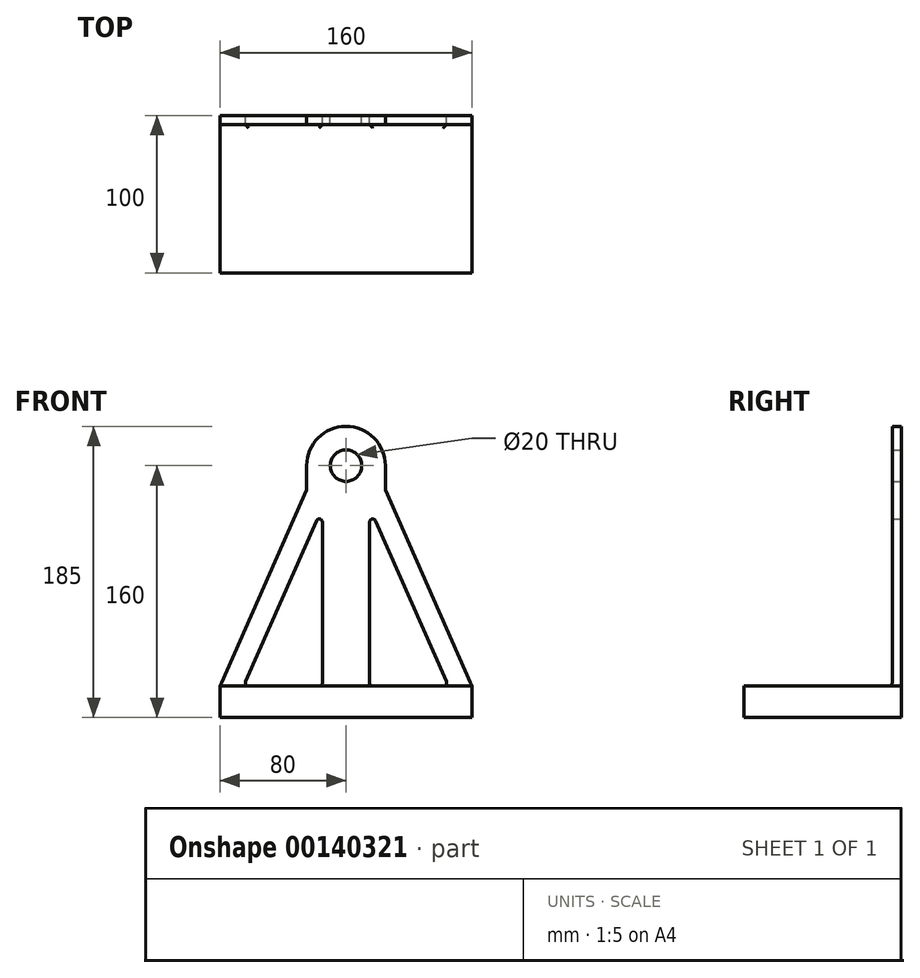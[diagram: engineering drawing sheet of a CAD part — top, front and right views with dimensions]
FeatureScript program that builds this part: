
annotation { "Feature Type Name" : "Feature", "Feature Type Description" : "" }
export const myFeature = defineFeature(function(context is Context, id is Id, definition is map)
    precondition{}
    {
        {
            var Q0;
            Q0=qCreatedBy(makeId("Front.planeOp"),FACE);
            var sketch = newSketch(context, id + "F0", { "sketchPlane" : qUnion([Q0])});
            skCircle(sketch, "E0", {"center": v(0, 160) * mm, "radius": 25 * mm, "construction": true});
            skLineSegment(sketch, "E1", {"start": v(-80, 0) * mm, "end": v(0, 0) * mm});
            skLineSegment(sketch, "E2", {"start": v(-80, 0) * mm, "end": v(-80, 20) * mm});
            skLineSegment(sketch, "E3", {"start": v(-25, 160) * mm, "end": v(-25, 0) * mm, "construction": true});
            skPoint(sketch, "E4", {"position": v(0, 185) * mm});
            skLineSegment(sketch, "E5", {"start": v(-80, 20) * mm, "end": v(-25, 20) * mm, "construction": true});
            skLineSegment(sketch, "E6", {"start": v(-25, 160) * mm, "end": v(-25, 145.42) * mm});
            skArc(sketch, "E7", {"start": v(0, 185) * mm, "mid": v(-17.68, 177.68) * mm, "end": v(-25, 160) * mm});
            skLineSegment(sketch, "E8", {"start": v(-80, 20) * mm, "end": v(-25.17, 144.62) * mm});
            skLineSegment(sketch, "E9.1", {"start": v(-61.93, 20) * mm, "end": v(-17, 20) * mm});
            skLineSegment(sketch, "E10", {"start": v(-15, 22) * mm, "end": v(-15, 124.12) * mm});
            skLineSegment(sketch, "E11.MirrorCS", {"start": v(80, 0) * mm, "end": v(0, 0) * mm});
            skLineSegment(sketch, "E12.MirrorCS", {"start": v(80, 0) * mm, "end": v(80, 20) * mm});
            skLineSegment(sketch, "E13.MirrorCS", {"start": v(80, 20) * mm, "end": v(25.17, 144.62) * mm});
            skLineSegment(sketch, "E14.MirrorCS", {"start": v(61.93, 20) * mm, "end": v(17, 20) * mm});
            skLineSegment(sketch, "E15.MirrorCS", {"start": v(15, 22) * mm, "end": v(15, 124.12) * mm});
            skLineSegment(sketch, "E16.MirrorCS", {"start": v(25, 160) * mm, "end": v(25, 145.42) * mm});
            skArc(sketch, "E17.MirrorCS", {"start": v(0, 185) * mm, "mid": v(17.68, 177.68) * mm, "end": v(25, 160) * mm});
            skCircle(sketch, "E18", {"center": v(0, 160) * mm, "radius": 10 * mm});
            skLineSegment(sketch, "E19", {"start": v(-63.77, 22.8) * mm, "end": v(-18.83, 124.93) * mm});
            skLineSegment(sketch, "E20.MirrorCS", {"start": v(63.77, 22.8) * mm, "end": v(18.83, 124.93) * mm});
            skPoint(sketch, "E21.visualSharp", {"position": v(-15, 20) * mm});
            skArc(sketch, "E21.filletArc", {"start": v(-17, 20) * mm, "mid": v(-15.59, 20.59) * mm, "end": v(-15, 22) * mm});
            skPoint(sketch, "E22.visualSharp", {"position": v(-65, 20) * mm});
            skArc(sketch, "E22.filletArc", {"start": v(-63.77, 22.8) * mm, "mid": v(-63.6, 20.9) * mm, "end": v(-61.93, 20) * mm});
            skPoint(sketch, "E23.visualSharp", {"position": v(-15, 133.64) * mm});
            skArc(sketch, "E23.filletArc", {"start": v(-15, 124.12) * mm, "mid": v(-16.59, 126.08) * mm, "end": v(-18.83, 124.93) * mm});
            skPoint(sketch, "E24.visualSharp", {"position": v(15, 133.64) * mm});
            skArc(sketch, "E24.filletArc", {"start": v(18.83, 124.93) * mm, "mid": v(16.59, 126.08) * mm, "end": v(15, 124.12) * mm});
            skPoint(sketch, "E25.visualSharp", {"position": v(15, 20) * mm});
            skArc(sketch, "E25.filletArc", {"start": v(15, 22) * mm, "mid": v(15.59, 20.59) * mm, "end": v(17, 20) * mm});
            skPoint(sketch, "E26.visualSharp", {"position": v(65, 20) * mm});
            skArc(sketch, "E26.filletArc", {"start": v(61.93, 20) * mm, "mid": v(63.6, 20.9) * mm, "end": v(63.77, 22.8) * mm});
            skPoint(sketch, "E27.visualSharp", {"position": v(80, 20) * mm});
            skPoint(sketch, "E28.visualSharp", {"position": v(-25, 145) * mm});
            skArc(sketch, "E28.filletArc", {"start": v(-25.17, 144.62) * mm, "mid": v(-25.04, 145) * mm, "end": v(-25, 145.42) * mm});
            skPoint(sketch, "E29.visualSharp", {"position": v(25, 145) * mm});
            skArc(sketch, "E29.filletArc", {"start": v(25, 145.42) * mm, "mid": v(25.04, 145) * mm, "end": v(25.17, 144.62) * mm});
            skLineSegment(sketch, "E30", {"start": v(-80, 20) * mm, "end": v(80, 20) * mm});
            skSolve(sketch);
        }
        {
            var Q0;
            Q0=makeQuery(id+"F0.imprint","IMPRINT",FACE,{"disambiguationData":[TD([[makeQuery(id+"F0.imprint","IMPRINT",EDGE,{"derivedFrom":sQuery(id+"F0.wireOp",EDGE,"E1")}),1.0]])]});
            var Q1;
            Q1=makeQuery(id+"F0.imprint","IMPRINT",FACE,{"disambiguationData":[TD([[makeQuery(id+"F0.imprint","IMPRINT",EDGE,{"derivedFrom":sQuery(id+"F0.wireOp",EDGE,"E6")}),1.0]])]});
            extrude(context, id + "F1", {"entities" : qUnion([Q0, Q1]), "depth" : 6 * mm});
        }
        {
            var Q0;
            Q0=makeQuery(id+"F0.imprint","IMPRINT",FACE,{"disambiguationData":[TD([[makeQuery(id+"F0.imprint","IMPRINT",EDGE,{"derivedFrom":sQuery(id+"F0.wireOp",EDGE,"E1")}),1.0]])]});
            extrude(context, id + "F2", {"entities" : qUnion([Q0]), "operationType" : NewBodyOperationType.ADD, "depth" : 100 * mm});
        }
        {
            var Q0;
            {var subQ0=sQuery(id+"F0.wireOp",EDGE,"E30");Q0=makeQuery(id+"F2.boolean.opBoolean","INTERSECT",EDGE,{"disambiguationData":[OD(2.0)],"derivedFrom":[makeQuery(id+"F1.opExtrude","CAP_FACE",FACE,{"disambiguationData":[OSD([sQuery(id+"F0.wireOp",EDGE,"E1"),sQuery(id+"F0.wireOp",EDGE,"E2"),sQuery(id+"F0.wireOp",EDGE,"E6"),sQuery(id+"F0.wireOp",EDGE,"E7"),sQuery(id+"F0.wireOp",EDGE,"E8"),sQuery(id+"F0.wireOp",EDGE,"E10"),sQuery(id+"F0.wireOp",EDGE,"E11.MirrorCS"),sQuery(id+"F0.wireOp",EDGE,"E12.MirrorCS"),sQuery(id+"F0.wireOp",EDGE,"E13.MirrorCS"),sQuery(id+"F0.wireOp",EDGE,"E15.MirrorCS"),sQuery(id+"F0.wireOp",EDGE,"E16.MirrorCS"),sQuery(id+"F0.wireOp",EDGE,"E17.MirrorCS"),sQuery(id+"F0.wireOp",EDGE,"E18"),sQuery(id+"F0.wireOp",EDGE,"E19"),sQuery(id+"F0.wireOp",EDGE,"E20.MirrorCS"),sQuery(id+"F0.wireOp",EDGE,"E21.filletArc"),sQuery(id+"F0.wireOp",EDGE,"E22.filletArc"),sQuery(id+"F0.wireOp",EDGE,"E23.filletArc"),sQuery(id+"F0.wireOp",EDGE,"E24.filletArc"),sQuery(id+"F0.wireOp",EDGE,"E25.filletArc"),sQuery(id+"F0.wireOp",EDGE,"E26.filletArc"),sQuery(id+"F0.wireOp",EDGE,"E28.filletArc"),sQuery(id+"F0.wireOp",EDGE,"E29.filletArc"),subQ0])],"isStart":false}),makeQuery(id+"F2.opExtrude","SWEPT_FACE",FACE,{"disambiguationData":[OSD([subQ0])]})]});}
            var Q1;
            {var subQ0=sQuery(id+"F0.wireOp",EDGE,"E30");Q1=makeQuery(id+"F2.boolean.opBoolean","INTERSECT",EDGE,{"disambiguationData":[OD(0.0)],"derivedFrom":[makeQuery(id+"F1.opExtrude","CAP_FACE",FACE,{"disambiguationData":[OSD([sQuery(id+"F0.wireOp",EDGE,"E1"),sQuery(id+"F0.wireOp",EDGE,"E2"),sQuery(id+"F0.wireOp",EDGE,"E6"),sQuery(id+"F0.wireOp",EDGE,"E7"),sQuery(id+"F0.wireOp",EDGE,"E8"),sQuery(id+"F0.wireOp",EDGE,"E10"),sQuery(id+"F0.wireOp",EDGE,"E11.MirrorCS"),sQuery(id+"F0.wireOp",EDGE,"E12.MirrorCS"),sQuery(id+"F0.wireOp",EDGE,"E13.MirrorCS"),sQuery(id+"F0.wireOp",EDGE,"E15.MirrorCS"),sQuery(id+"F0.wireOp",EDGE,"E16.MirrorCS"),sQuery(id+"F0.wireOp",EDGE,"E17.MirrorCS"),sQuery(id+"F0.wireOp",EDGE,"E18"),sQuery(id+"F0.wireOp",EDGE,"E19"),sQuery(id+"F0.wireOp",EDGE,"E20.MirrorCS"),sQuery(id+"F0.wireOp",EDGE,"E21.filletArc"),sQuery(id+"F0.wireOp",EDGE,"E22.filletArc"),sQuery(id+"F0.wireOp",EDGE,"E23.filletArc"),sQuery(id+"F0.wireOp",EDGE,"E24.filletArc"),sQuery(id+"F0.wireOp",EDGE,"E25.filletArc"),sQuery(id+"F0.wireOp",EDGE,"E26.filletArc"),sQuery(id+"F0.wireOp",EDGE,"E28.filletArc"),sQuery(id+"F0.wireOp",EDGE,"E29.filletArc"),subQ0])],"isStart":false}),makeQuery(id+"F2.opExtrude","SWEPT_FACE",FACE,{"disambiguationData":[OSD([subQ0])]})]});}
            var Q2;
            {var subQ0=sQuery(id+"F0.wireOp",EDGE,"E30");Q2=makeQuery(id+"F2.boolean.opBoolean","INTERSECT",EDGE,{"disambiguationData":[OD(1.0)],"derivedFrom":[makeQuery(id+"F1.opExtrude","CAP_FACE",FACE,{"disambiguationData":[OSD([sQuery(id+"F0.wireOp",EDGE,"E1"),sQuery(id+"F0.wireOp",EDGE,"E2"),sQuery(id+"F0.wireOp",EDGE,"E6"),sQuery(id+"F0.wireOp",EDGE,"E7"),sQuery(id+"F0.wireOp",EDGE,"E8"),sQuery(id+"F0.wireOp",EDGE,"E10"),sQuery(id+"F0.wireOp",EDGE,"E11.MirrorCS"),sQuery(id+"F0.wireOp",EDGE,"E12.MirrorCS"),sQuery(id+"F0.wireOp",EDGE,"E13.MirrorCS"),sQuery(id+"F0.wireOp",EDGE,"E15.MirrorCS"),sQuery(id+"F0.wireOp",EDGE,"E16.MirrorCS"),sQuery(id+"F0.wireOp",EDGE,"E17.MirrorCS"),sQuery(id+"F0.wireOp",EDGE,"E18"),sQuery(id+"F0.wireOp",EDGE,"E19"),sQuery(id+"F0.wireOp",EDGE,"E20.MirrorCS"),sQuery(id+"F0.wireOp",EDGE,"E21.filletArc"),sQuery(id+"F0.wireOp",EDGE,"E22.filletArc"),sQuery(id+"F0.wireOp",EDGE,"E23.filletArc"),sQuery(id+"F0.wireOp",EDGE,"E24.filletArc"),sQuery(id+"F0.wireOp",EDGE,"E25.filletArc"),sQuery(id+"F0.wireOp",EDGE,"E26.filletArc"),sQuery(id+"F0.wireOp",EDGE,"E28.filletArc"),sQuery(id+"F0.wireOp",EDGE,"E29.filletArc"),subQ0])],"isStart":false}),makeQuery(id+"F2.opExtrude","SWEPT_FACE",FACE,{"disambiguationData":[OSD([subQ0])]})]});}
            fillet(context, id + "F3", {"entities" : qUnion([Q0, Q1, Q2]), "radius" : 2 * mm, "tangentPropagation" : true, "allowEdgeOverflow" : false});
        }
    });
